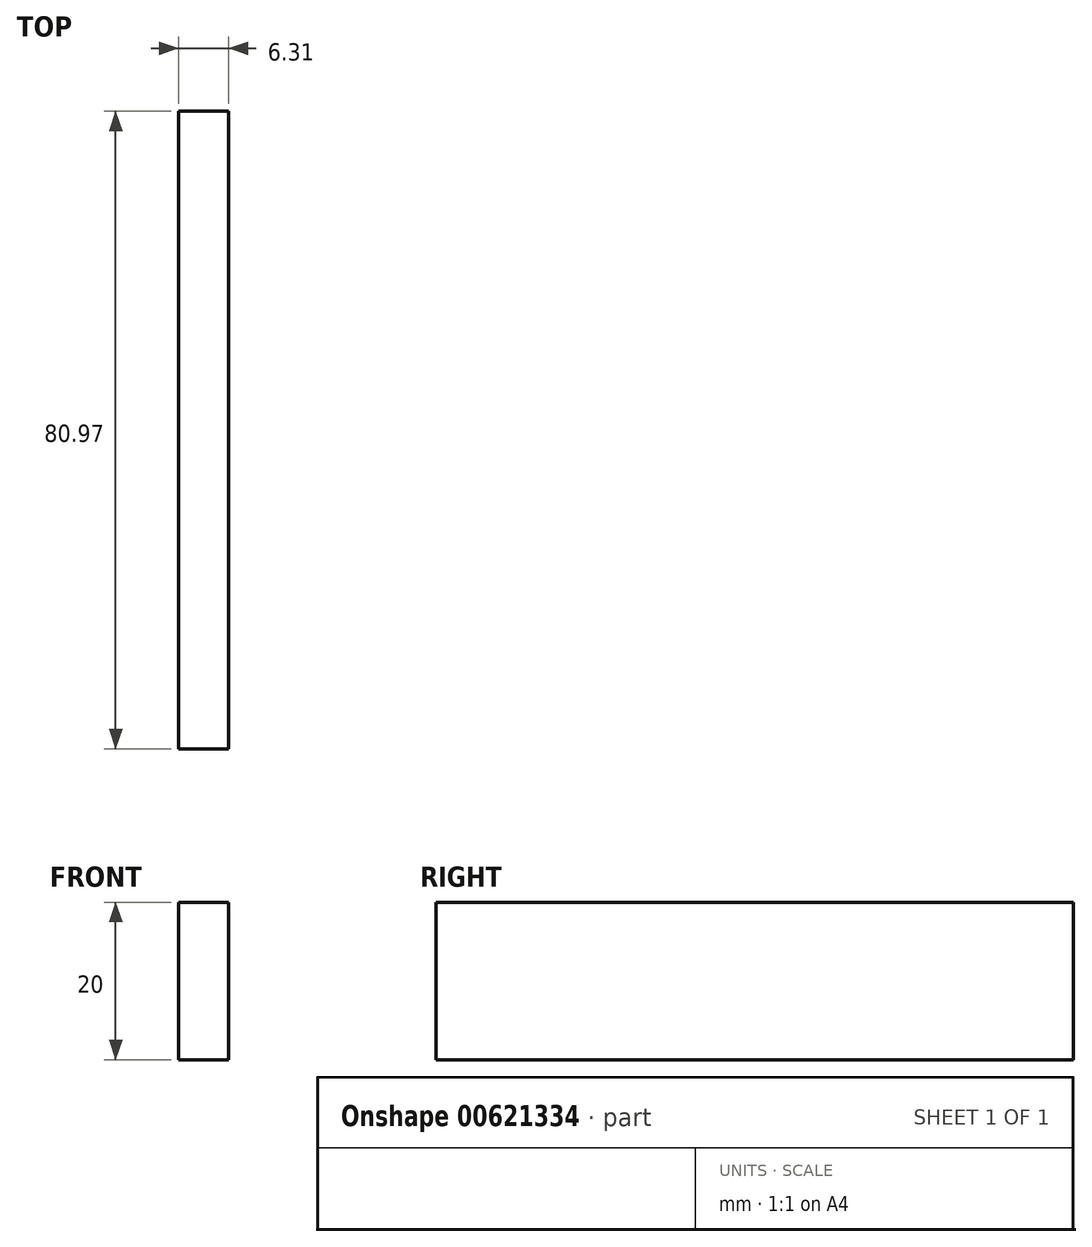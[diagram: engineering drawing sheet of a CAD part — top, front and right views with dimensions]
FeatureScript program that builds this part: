
annotation { "Feature Type Name" : "Feature", "Feature Type Description" : "" }
export const myFeature = defineFeature(function(context is Context, id is Id, definition is map)
    precondition{}
    {
        {
            var Q0;
            Q0=qCreatedBy(makeId("Top.planeOp"),FACE);
            var sketch = newSketch(context, id + "F0", { "sketchPlane" : qUnion([Q0])});
            skLineSegment(sketch, "E0.bottom", {"start": v(-38.13, -58.5) * mm, "end": v(-31.82, -58.5) * mm});
            skLineSegment(sketch, "E0.top", {"start": v(-38.13, 22.47) * mm, "end": v(-31.82, 22.47) * mm});
            skLineSegment(sketch, "E0.left", {"start": v(-38.13, -58.5) * mm, "end": v(-38.13, 22.47) * mm});
            skLineSegment(sketch, "E0.right", {"start": v(-31.82, -58.5) * mm, "end": v(-31.82, 22.47) * mm});
            skSolve(sketch);
        }
        {
            var Q0;
            Q0 = qSketchRegion(id + "F0", true);
            extrude(context, id + "F1", {"entities" : qUnion([Q0]), "depth" : 20 * mm, "offsetDistance" : 25.4 * mm});
        }
    });
